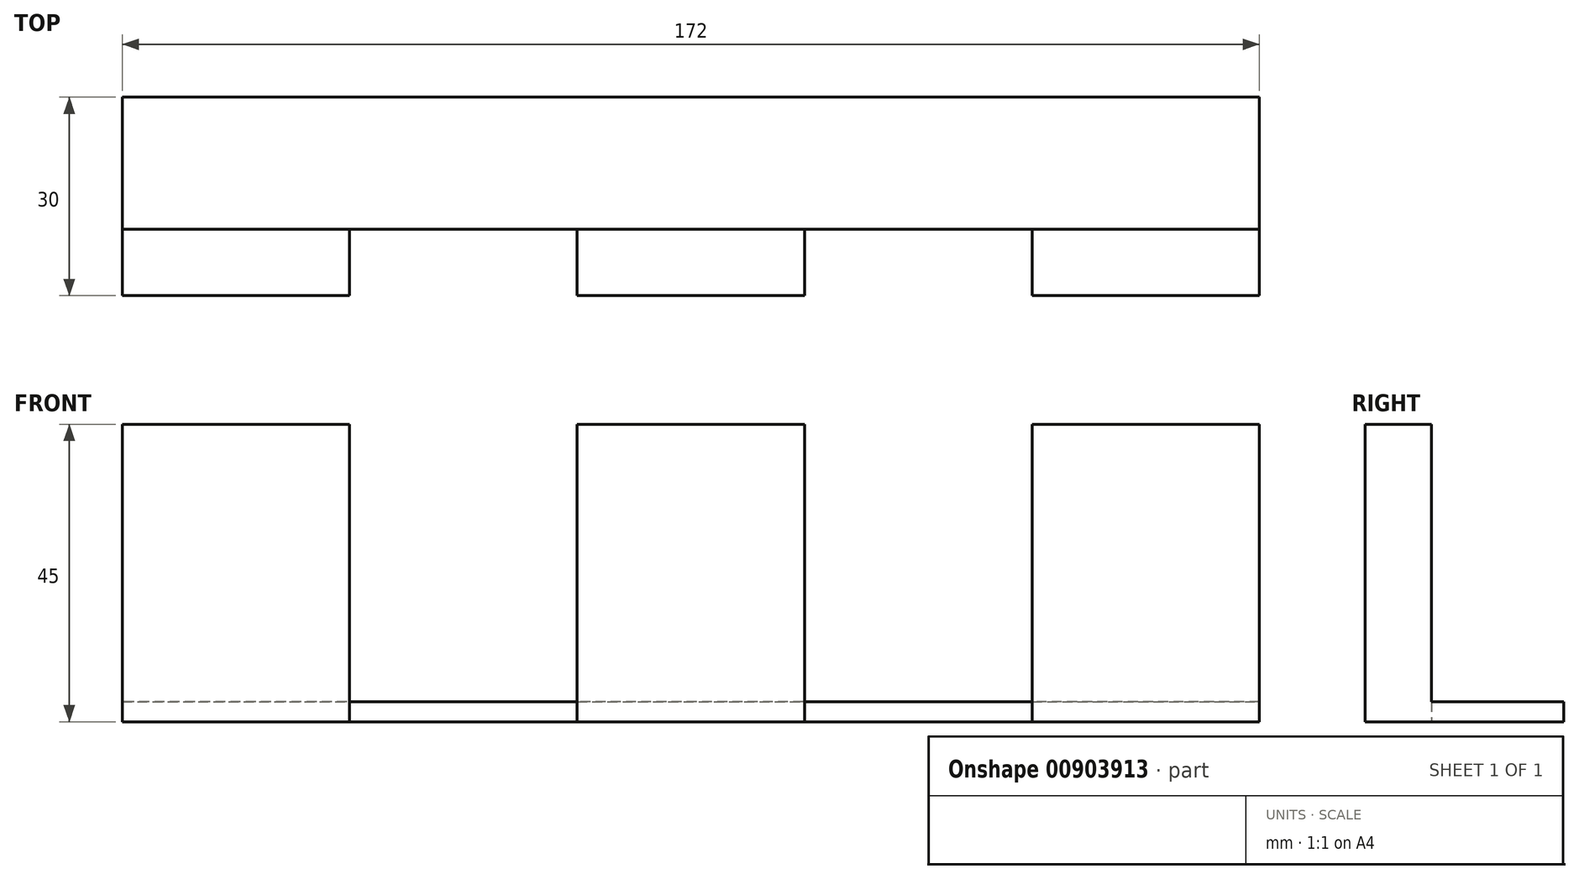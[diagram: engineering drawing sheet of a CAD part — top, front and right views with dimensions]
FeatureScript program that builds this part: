
annotation { "Feature Type Name" : "Feature", "Feature Type Description" : "" }
export const myFeature = defineFeature(function(context is Context, id is Id, definition is map)
    precondition{}
    {
        {
            var Q0;
            Q0=qCreatedBy(makeId("Top.planeOp"),FACE);
            var sketch = newSketch(context, id + "F0", { "sketchPlane" : qUnion([Q0])});
            skLineSegment(sketch, "E0.bottom", {"start": v(86, 15) * mm, "end": v(-86, 15) * mm});
            skLineSegment(sketch, "E0.top", {"start": v(86, -15) * mm, "end": v(-86, -15) * mm});
            skLineSegment(sketch, "E0.left", {"start": v(86, 15) * mm, "end": v(86, -15) * mm});
            skLineSegment(sketch, "E0.right", {"start": v(-86, 15) * mm, "end": v(-86, -15) * mm});
            skPoint(sketch, "E0.middle", {"position": v(0, 0) * mm});
            skLineSegment(sketch, "E1", {"start": v(-86, -15) * mm, "end": v(-51.6, -15) * mm});
            skLineSegment(sketch, "E2", {"start": v(-51.6, -15) * mm, "end": v(-17.2, -15) * mm});
            skLineSegment(sketch, "E3", {"start": v(-17.2, -15) * mm, "end": v(17.2, -15) * mm});
            skLineSegment(sketch, "E4", {"start": v(17.2, -15) * mm, "end": v(51.6, -15) * mm});
            skLineSegment(sketch, "E5", {"start": v(51.6, -15) * mm, "end": v(86, -15) * mm});
            skLineSegment(sketch, "E6", {"start": v(-86, -15) * mm, "end": v(-86, -5) * mm});
            skLineSegment(sketch, "E7", {"start": v(-86, -5) * mm, "end": v(86, -5) * mm});
            skLineSegment(sketch, "E8", {"start": v(-51.6, -15) * mm, "end": v(-51.6, -5) * mm});
            skLineSegment(sketch, "E9", {"start": v(-17.2, -15) * mm, "end": v(-17.2, -5) * mm});
            skLineSegment(sketch, "E10", {"start": v(17.2, -15) * mm, "end": v(17.2, -5) * mm});
            skLineSegment(sketch, "E11", {"start": v(51.6, -15) * mm, "end": v(51.6, -5) * mm});
            skSolve(sketch);
        }
        {
            var Q0;
            {var subQ1=sQuery(id+"F0.wireOp",EDGE,"E0.bottom");Q0=makeQuery(id+"F0.imprint","IMPRINT",FACE,{"disambiguationData":[TD([[makeQuery(id+"F0.imprint","IMPRINT",EDGE,{"derivedFrom":subQ1}),1.0]])]});}
            extrude(context, id + "F1", {"entities" : qUnion([Q0]), "depth" : 3 * mm, "offsetDistance" : 25 * mm});
        }
        {
            var Q0;
            {var subQ3=sQuery(id+"F0.wireOp",EDGE,"E8");Q0=makeQuery(id+"F0.imprint","IMPRINT",FACE,{"disambiguationData":[TD([[makeQuery(id+"F0.imprint","IMPRINT",EDGE,{"derivedFrom":subQ3}),1.0]])]});}
            var Q1;
            {var subQ0=sQuery(id+"F0.wireOp",EDGE,"E9");Q1=makeQuery(id+"F0.imprint","IMPRINT",FACE,{"disambiguationData":[TD([[makeQuery(id+"F0.imprint","IMPRINT",EDGE,{"derivedFrom":subQ0}),-1.0]])]});}
            var Q2;
            {var subQ3=sQuery(id+"F0.wireOp",EDGE,"E11");Q2=makeQuery(id+"F0.imprint","IMPRINT",FACE,{"disambiguationData":[TD([[makeQuery(id+"F0.imprint","IMPRINT",EDGE,{"derivedFrom":subQ3}),-1.0]])]});}
            extrude(context, id + "F2", {"entities" : qUnion([Q0, Q1, Q2]), "operationType" : NewBodyOperationType.ADD, "depth" : 45 * mm, "offsetDistance" : 25 * mm});
        }
    });
